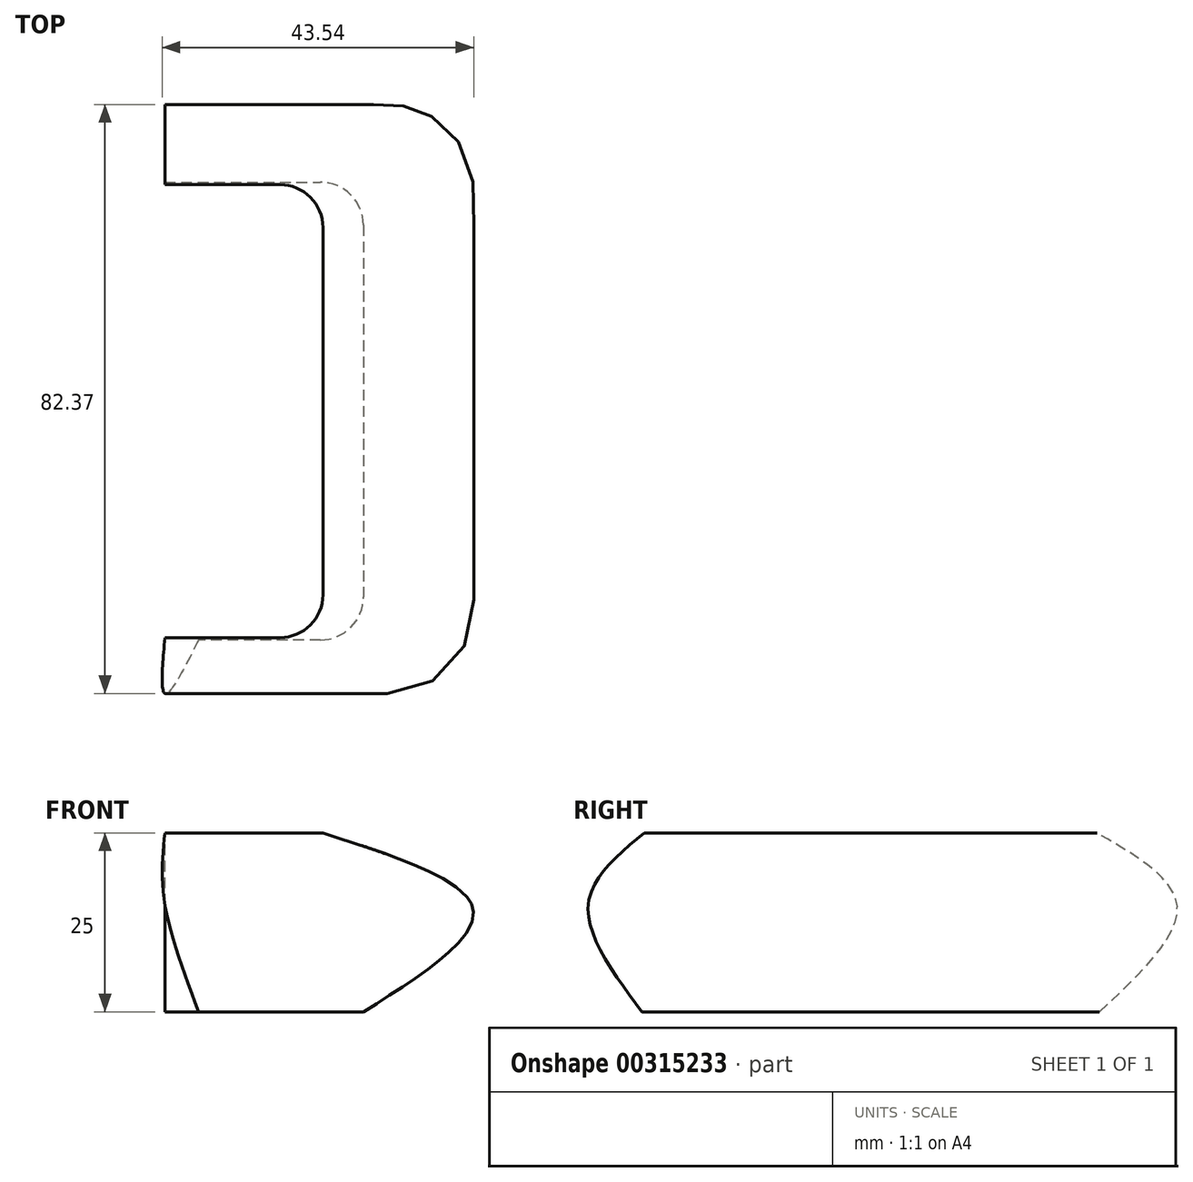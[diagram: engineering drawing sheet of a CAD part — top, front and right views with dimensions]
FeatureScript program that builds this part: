
annotation { "Feature Type Name" : "Feature", "Feature Type Description" : "" }
export const myFeature = defineFeature(function(context is Context, id is Id, definition is map)
    precondition{}
    {
        {
            var Q0;
            Q0=qCreatedBy(makeId("Top.planeOp"),FACE);
            cPlane(context, id + "F0", {"entities" : qUnion([Q0]), "cplaneType" : CPlaneType.OFFSET, "offset" : 15 * mm, "width" : 150 * mm, "height" : 150 * mm});
        }
        {
            var Q0;
            Q0=qCreatedBy(makeId("Top.planeOp"),FACE);
            cPlane(context, id + "F1", {"entities" : qUnion([Q0]), "cplaneType" : CPlaneType.OFFSET, "offset" : 25 * mm, "width" : 150 * mm, "height" : 150 * mm});
        }
        {
            var Q0;
            Q0=qCreatedBy(makeId("Top.planeOp"),FACE);
            var sketch = newSketch(context, id + "F2", { "sketchPlane" : qUnion([Q0])});
            skLineSegment(sketch, "E0", {"start": v(0, 35.06) * mm, "end": v(21.76, 35.06) * mm});
            skLineSegment(sketch, "E1", {"start": v(27.76, 29.06) * mm, "end": v(27.76, -22.94) * mm});
            skLineSegment(sketch, "E2", {"start": v(21.76, -28.94) * mm, "end": v(4.73, -28.94) * mm});
            skPoint(sketch, "E3.visualSharp", {"position": v(27.76, 35.06) * mm});
            skArc(sketch, "E3.filletArc", {"start": v(27.76, 29.06) * mm, "mid": v(26, 33.3) * mm, "end": v(21.76, 35.06) * mm});
            skPoint(sketch, "E4.visualSharp", {"position": v(27.76, -28.94) * mm});
            skArc(sketch, "E4.filletArc", {"start": v(21.76, -28.94) * mm, "mid": v(26, -27.19) * mm, "end": v(27.76, -22.94) * mm});
            skSolve(sketch);
        }
        {
            var Q0;
            Q0=qCreatedBy(id+"F0.planeOp",FACE);
            var sketch = newSketch(context, id + "F3", { "sketchPlane" : qUnion([Q0])});
            skLineSegment(sketch, "E5", {"start": v(0, 45.9) * mm, "end": v(30.92, 45.9) * mm});
            skLineSegment(sketch, "E6", {"start": v(42.92, 33.9) * mm, "end": v(42.92, -24.41) * mm});
            skLineSegment(sketch, "E7", {"start": v(30.92, -36.41) * mm, "end": v(0, -36.41) * mm});
            skPoint(sketch, "E8.visualSharp", {"position": v(42.92, 45.9) * mm});
            skArc(sketch, "E8.filletArc", {"start": v(42.92, 33.9) * mm, "mid": v(39.4, 42.38) * mm, "end": v(30.92, 45.9) * mm});
            skPoint(sketch, "E9.visualSharp", {"position": v(42.92, -36.41) * mm});
            skArc(sketch, "E9.filletArc", {"start": v(30.92, -36.41) * mm, "mid": v(39.4, -32.9) * mm, "end": v(42.92, -24.41) * mm});
            skSolve(sketch);
        }
        {
            var Q0;
            Q0=qCreatedBy(id+"F1.planeOp",FACE);
            var sketch = newSketch(context, id + "F4", { "sketchPlane" : qUnion([Q0])});
            skLineSegment(sketch, "E10", {"start": v(0, 34.72) * mm, "end": v(16.11, 34.72) * mm});
            skLineSegment(sketch, "E11", {"start": v(22.11, 28.72) * mm, "end": v(22.11, -22.62) * mm});
            skLineSegment(sketch, "E12", {"start": v(16.11, -28.62) * mm, "end": v(0, -28.62) * mm});
            skPoint(sketch, "E13.visualSharp", {"position": v(22.11, 34.72) * mm});
            skArc(sketch, "E13.filletArc", {"start": v(22.11, 28.72) * mm, "mid": v(20.36, 32.96) * mm, "end": v(16.11, 34.72) * mm});
            skPoint(sketch, "E14.visualSharp", {"position": v(22.11, -28.62) * mm});
            skArc(sketch, "E14.filletArc", {"start": v(16.11, -28.62) * mm, "mid": v(20.36, -26.86) * mm, "end": v(22.11, -22.62) * mm});
            skSolve(sketch);
        }
        {
            var Q0;
            Q0 = qConstructionFilter(qBodyType(qCreatedBy(id + "F2" ,EDGE), BodyType.WIRE), ConstructionObject.NO);
            var Q1;
            Q1 = qConstructionFilter(qBodyType(qCreatedBy(id + "F3" ,EDGE), BodyType.WIRE), ConstructionObject.NO);
            var Q2;
            Q2 = qConstructionFilter(qBodyType(qCreatedBy(id + "F4" ,EDGE), BodyType.WIRE), ConstructionObject.NO);
            loft(context, id + "F5", {"bodyType" : ToolBodyType.SURFACE, "wireProfilesArray" : [{ "wireProfileEntities" : qUnion([Q0]) }, { "wireProfileEntities" : qUnion([Q1]) }, { "wireProfileEntities" : qUnion([Q2]) }]});
        }
    });
